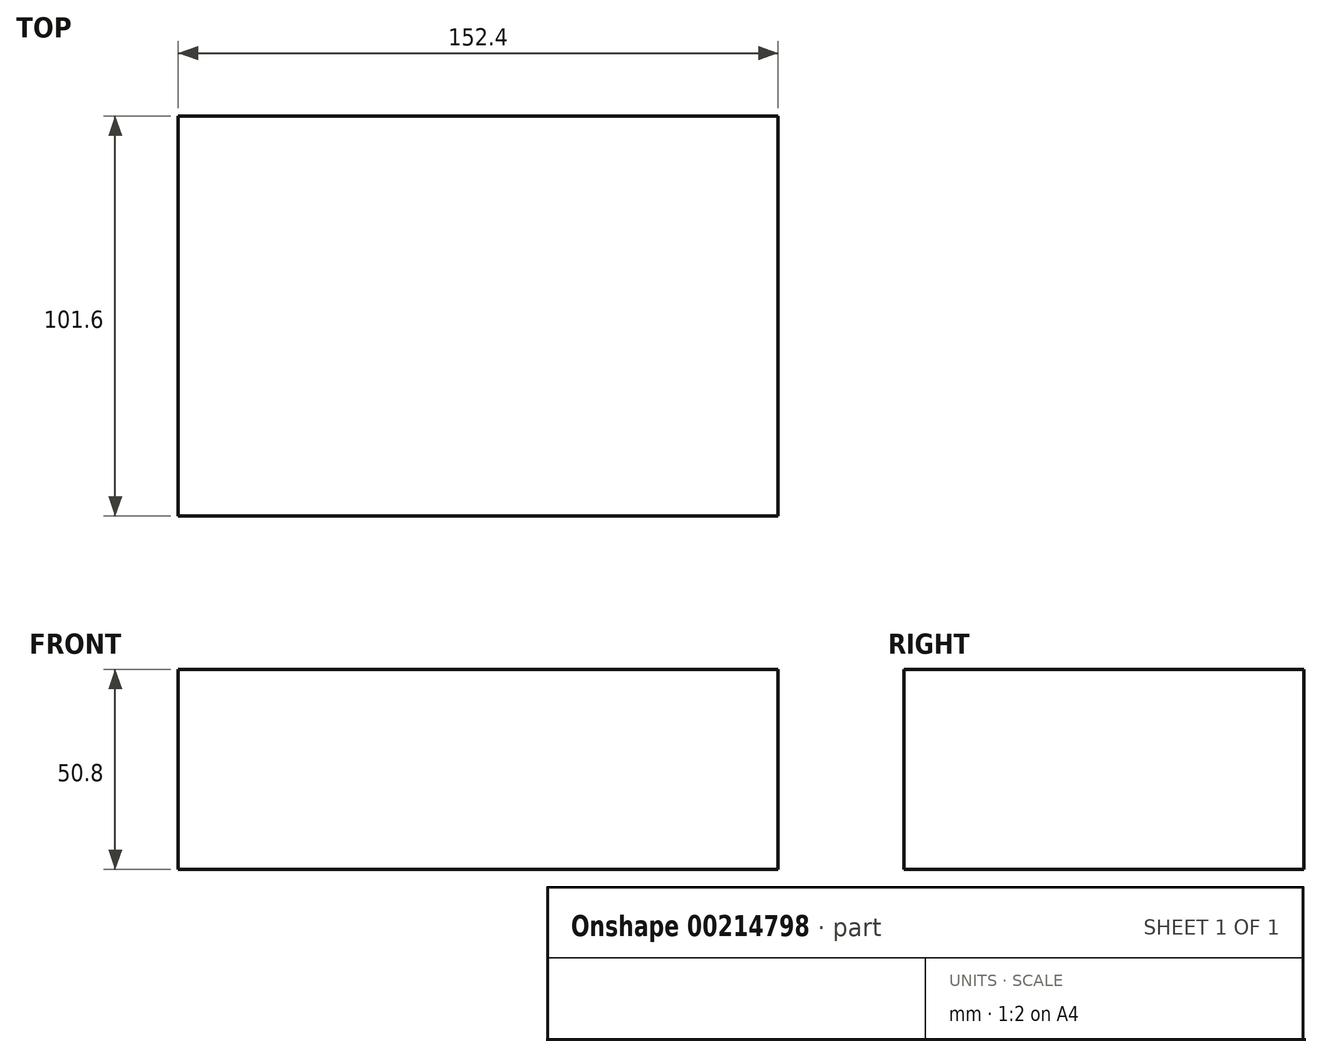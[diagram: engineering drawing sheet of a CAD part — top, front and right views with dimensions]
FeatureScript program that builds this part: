
annotation { "Feature Type Name" : "Feature", "Feature Type Description" : "" }
export const myFeature = defineFeature(function(context is Context, id is Id, definition is map)
    precondition{}
    {
        {
            var Q0;
            Q0=qCreatedBy(makeId("Top.planeOp"),FACE);
            var sketch = newSketch(context, id + "F0", { "sketchPlane" : qUnion([Q0])});
            skLineSegment(sketch, "E0.bottom", {"start": v(0, 0) * mm, "end": v(152.4, 0) * mm});
            skLineSegment(sketch, "E0.top", {"start": v(0, -101.6) * mm, "end": v(152.4, -101.6) * mm});
            skLineSegment(sketch, "E0.left", {"start": v(0, 0) * mm, "end": v(0, -101.6) * mm});
            skLineSegment(sketch, "E0.right", {"start": v(152.4, 0) * mm, "end": v(152.4, -101.6) * mm});
            skSolve(sketch);
        }
        {
            var Q0;
            Q0=makeQuery(id+"F0.imprint","IMPRINT",FACE,{"disambiguationData":[TD([[makeQuery(id+"F0.imprint","IMPRINT",EDGE,{"derivedFrom":sQuery(id+"F0.wireOp",EDGE,"E0.bottom")}),-1.0]])]});
            extrude(context, id + "F1", {"entities" : qUnion([Q0]), "depth" : 50.8 * mm});
        }
    });
